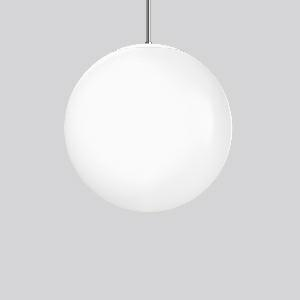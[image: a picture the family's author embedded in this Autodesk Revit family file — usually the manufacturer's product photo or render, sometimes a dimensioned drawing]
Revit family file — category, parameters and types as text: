
# Revit family: basic_ball_312126_002_76_7ddf
name_source: partatom
category: Lighting Fixtures
units: mm (PartAtom-declared; Revit-internal decimal feet)

## family parameters
Cut with Voids When Loaded = No
Host = Face
Light Source = No
Part Type = Normal
Room Calculation Point = No
Round Connector Dimension = Use Diameter
Shared = No

## types (1)
- BASIC BALL (1 x LED Modul 930, 9350 lm, 3000)
    Apparent Load = 79 VA
    CIE Flux Codes = 26 51 76 56 100
    Color Rendering = 90
    Color Temperature = 3000
    Default Elevation = 1800 mm
    Description = Series: BASIC BALL
Pendant luminaire in timelessly classic sphere design. Base: metal, chrome. Canopy: metal, chrome-plated. Diffuser: shockproof plastic (polyethylene), opal, satin finish. Shadow-free, homogeneous and soft illumination. Incl. mounting plate with connecting terminal and mounting material for pendant tube. Pendant tube must be ordered separately! 
Colour: white
Diameter: 500 mm
Height: 500 mm
Lamp: LED
Socket: without socket
Colour temperature: 3000K
Colour rendering index (CRI): 90
System power: 79 W
Rated luminous flux: 9350 lm
Luminous efficiency: 118 lm/W
Control gear: Converter, dimmable, DALI
Protection class: I
Type of protection: IP 40
    Height = 500 mm
    Lamp = 1 x LED Modul 930
    Lamp Light Flux = 9350 lm
    Lamp count = 1
    Length = 500 mm
    Lifetime = 50000 h
    Luminous efficacy = 118 lm/W
    Manufacturer = RZB
    ModVariant = No
    Model = 312126.002.76
    Mounting Place = Ceiling
    Mounting Type = Pendant
    Number of Poles = 1
    OnlyDefault = Yes
    Power Factor = 1
    Product Name = BASIC BALL
    Product group = Pendant luminaires
    ProductGroupID = 902
    Protection Class = Protection class I
    Protection Degree = IP 40
    RLX_Detail_Level = 1
    RLX_Emergency_Light_Flux = 0 lm
    RLX_Emergency_Type = 0
    RLX_Emergency_Type_DB = No
    RlxData = <blob elided: 53865 chars, md5=edaa1301>
    Socket = socket
    Standby Power = 0 W
    System Light Flux = 9350 lm
    System Power = 79 W
    Type Comments = Product without accessories
    Type Image = 312126.002.jpg
    URL = http://relux.com
    VarID = ---
    Voltage = 230 V
    Voltage Range = 220-240 V
    Weight = 0.00 kg
    Width = 0 mm  [stored 0 ft]

note: [stored X ft] marks values corroborated as IEEE doubles in the binary element streams (Revit-internal decimal feet)

## geometry (parser evidence)
native form markers: Blend x4, Sweep x14
no freeform markers — native parametric forms only
